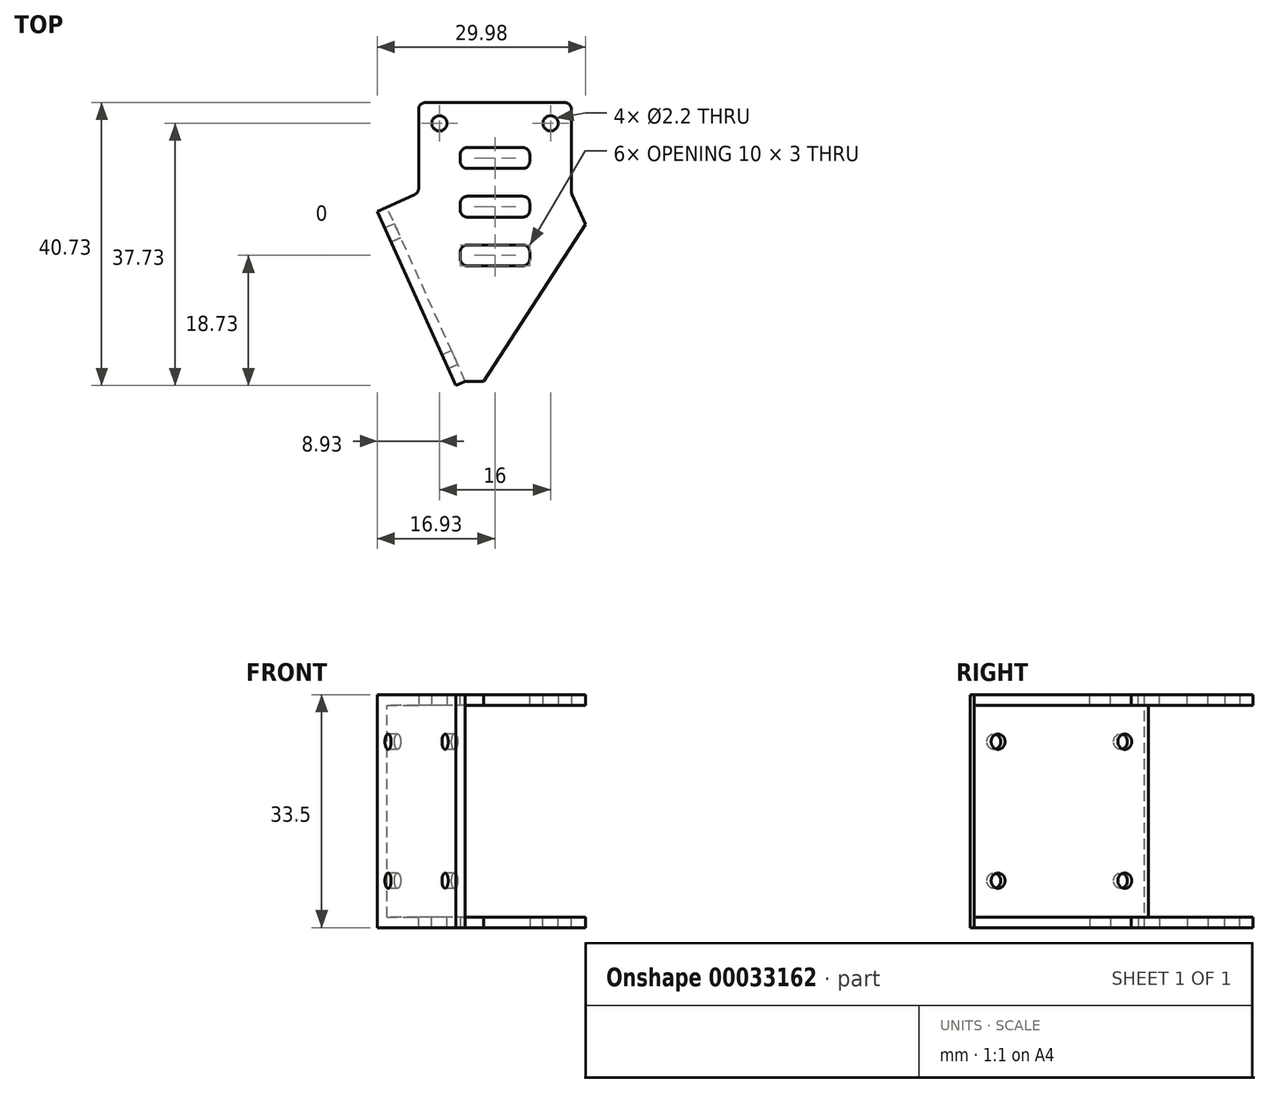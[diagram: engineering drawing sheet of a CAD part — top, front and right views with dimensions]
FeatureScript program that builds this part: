
annotation { "Feature Type Name" : "Feature", "Feature Type Description" : "" }
export const myFeature = defineFeature(function(context is Context, id is Id, definition is map)
    precondition{}
    {
        {
            var Q0;
            Q0=qCreatedBy(makeId("Top.planeOp"),FACE);
            var sketch = newSketch(context, id + "F0", { "sketchPlane" : qUnion([Q0])});
            skLineSegment(sketch, "E0.bottom", {"start": v(11, 16.5) * mm, "end": v(-11, 16.5) * mm});
            skLineSegment(sketch, "E0.top", {"start": v(11, -16.5) * mm, "end": v(-11, -16.5) * mm});
            skLineSegment(sketch, "E0.left", {"start": v(11, 16.5) * mm, "end": v(11, -16.5) * mm});
            skLineSegment(sketch, "E0.right", {"start": v(-11, 16.5) * mm, "end": v(-11, -16.5) * mm});
            skPoint(sketch, "E0.middle", {"position": v(0, 0) * mm});
            skCircle(sketch, "E1", {"center": v(8, 13.5) * mm, "radius": 1.1 * mm});
            skCircle(sketch, "E2.MirrorC", {"center": v(-8, 13.5) * mm, "radius": 1.1 * mm});
            skLineSegment(sketch, "E3", {"start": v(-11, 3.5) * mm, "end": v(-2, -16.5) * mm});
            skLineSegment(sketch, "E4.1.0.0", {"start": v(11, 3.5) * mm, "end": v(20, -16.5) * mm});
            skLineSegment(sketch, "E4.direction1", {"start": v(-2, -16.5) * mm, "end": v(20, -16.5) * mm, "construction": true});
            skLineSegment(sketch, "E5", {"start": v(11, -16.5) * mm, "end": v(20, -16.5) * mm});
            skSolve(sketch);
        }
        {
            var Q0;
            {var subQ4=sQuery(id+"F0.wireOp",EDGE,"E0.bottom");Q0=makeQuery(id+"F0.imprint","IMPRINT",FACE,{"disambiguationData":[TD([[makeQuery(id+"F0.imprint","IMPRINT",EDGE,{"derivedFrom":subQ4}),1.0]])]});}
            var Q1;
            {var subQ2=sQuery(id+"F0.wireOp",EDGE,"E4.1.0.0");Q1=makeQuery(id+"F0.imprint","IMPRINT",FACE,{"disambiguationData":[TD([[makeQuery(id+"F0.imprint","IMPRINT",EDGE,{"derivedFrom":subQ2}),-1.0]])]});}
            extrude(context, id + "F1", {"entities" : qUnion([Q0, Q1]), "depth" : 1.5 * mm});
        }
        {
            var Q0;
            Q0=makeQuery(id+"F1.opExtrude","CAP_FACE",FACE,{"disambiguationData":[OSD([sQuery(id+"F0.wireOp",EDGE,"E0.bottom"),sQuery(id+"F0.wireOp",EDGE,"E0.top"),sQuery(id+"F0.wireOp",EDGE,"E0.left"),sQuery(id+"F0.wireOp",EDGE,"E0.right"),sQuery(id+"F0.wireOp",EDGE,"E1"),sQuery(id+"F0.wireOp",EDGE,"E2.MirrorC"),sQuery(id+"F0.wireOp",EDGE,"E3"),sQuery(id+"F0.wireOp",EDGE,"E4.1.0.0"),sQuery(id+"F0.wireOp",EDGE,"E5")])],"isStart":false});
            var sketch = newSketch(context, id + "F2", { "sketchPlane" : qUnion([Q0])});
            skLineSegment(sketch, "E6", {"start": v(3, -16.5) * mm, "end": v(13.05, -1.06) * mm});
            skLineSegment(sketch, "E7", {"start": v(0, 16.5) * mm, "end": v(0, -16.5) * mm, "construction": true});
            skLineSegment(sketch, "E8.bottom", {"start": v(-4, 10) * mm, "end": v(4, 10) * mm});
            skLineSegment(sketch, "E8.top", {"start": v(-4, 7) * mm, "end": v(4, 7) * mm});
            skLineSegment(sketch, "E8.left", {"start": v(-5, 9) * mm, "end": v(-5, 8) * mm});
            skLineSegment(sketch, "E8.right", {"start": v(5, 9) * mm, "end": v(5, 8) * mm});
            skPoint(sketch, "E8.middle", {"position": v(0, 8.5) * mm});
            skPoint(sketch, "E9", {"position": v(-8, 13.5) * mm});
            skPoint(sketch, "E10.visualSharp", {"position": v(-5, 10) * mm});
            skArc(sketch, "E10.filletArc", {"start": v(-4, 10) * mm, "mid": v(-4.7, 9.7) * mm, "end": v(-5, 9) * mm});
            skPoint(sketch, "E11.visualSharp", {"position": v(-5, 7) * mm});
            skArc(sketch, "E11.filletArc", {"start": v(-5, 8) * mm, "mid": v(-4.7, 7.3) * mm, "end": v(-4, 7) * mm});
            skPoint(sketch, "E12.visualSharp", {"position": v(5, 10) * mm});
            skArc(sketch, "E12.filletArc", {"start": v(5, 9) * mm, "mid": v(4.7, 9.7) * mm, "end": v(4, 10) * mm});
            skPoint(sketch, "E13.visualSharp", {"position": v(5, 7) * mm});
            skArc(sketch, "E13.filletArc", {"start": v(4, 7) * mm, "mid": v(4.7, 7.3) * mm, "end": v(5, 8) * mm});
            skPoint(sketch, "E14.1.0.0", {"position": v(5, 3) * mm});
            skPoint(sketch, "E14.1.0.1", {"position": v(0, 1.5) * mm});
            skPoint(sketch, "E14.1.0.2", {"position": v(-5, 3) * mm});
            skPoint(sketch, "E14.1.0.3", {"position": v(-5, 0) * mm});
            skPoint(sketch, "E14.1.0.4", {"position": v(5, 0) * mm});
            skLineSegment(sketch, "E14.1.0.5", {"start": v(-4, 3) * mm, "end": v(4, 3) * mm});
            skLineSegment(sketch, "E14.1.0.6", {"start": v(-4, 0) * mm, "end": v(4, 0) * mm});
            skArc(sketch, "E14.1.0.7", {"start": v(4, 0) * mm, "mid": v(4.7, 0.3) * mm, "end": v(5, 1) * mm});
            skArc(sketch, "E14.1.0.8", {"start": v(5, 2) * mm, "mid": v(4.7, 2.7) * mm, "end": v(4, 3) * mm});
            skArc(sketch, "E14.1.0.9", {"start": v(-5, 1) * mm, "mid": v(-4.7, 0.3) * mm, "end": v(-4, 0) * mm});
            skLineSegment(sketch, "E14.1.0.10", {"start": v(-5, 2) * mm, "end": v(-5, 1) * mm});
            skLineSegment(sketch, "E14.1.0.11", {"start": v(5, 2) * mm, "end": v(5, 1) * mm});
            skArc(sketch, "E14.1.0.12", {"start": v(-4, 3) * mm, "mid": v(-4.7, 2.7) * mm, "end": v(-5, 2) * mm});
            skLineSegment(sketch, "E14.direction1", {"start": v(-5, 7) * mm, "end": v(-5, 0) * mm, "construction": true});
            skPoint(sketch, "E15.0.2.0", {"position": v(5, -4) * mm});
            skPoint(sketch, "E15.1.2.0", {"position": v(0, -5.5) * mm});
            skPoint(sketch, "E15.2.2.0", {"position": v(-5, -4) * mm});
            skPoint(sketch, "E15.3.2.0", {"position": v(-5, -7) * mm});
            skPoint(sketch, "E15.4.2.0", {"position": v(5, -7) * mm});
            skLineSegment(sketch, "E15.5.2.0", {"start": v(-4, -4) * mm, "end": v(4, -4) * mm});
            skLineSegment(sketch, "E15.8.2.0", {"start": v(-4, -7) * mm, "end": v(4, -7) * mm});
            skArc(sketch, "E15.11.2.0", {"start": v(4, -7) * mm, "mid": v(4.7, -6.7) * mm, "end": v(5, -6) * mm});
            skArc(sketch, "E15.15.2.0", {"start": v(5, -5) * mm, "mid": v(4.7, -4.3) * mm, "end": v(4, -4) * mm});
            skArc(sketch, "E15.19.2.0", {"start": v(-5, -6) * mm, "mid": v(-4.7, -6.7) * mm, "end": v(-4, -7) * mm});
            skLineSegment(sketch, "E15.23.2.0", {"start": v(-5, -5) * mm, "end": v(-5, -6) * mm});
            skLineSegment(sketch, "E15.26.2.0", {"start": v(5, -5) * mm, "end": v(5, -6) * mm});
            skArc(sketch, "E15.29.2.0", {"start": v(-4, -4) * mm, "mid": v(-4.7, -4.3) * mm, "end": v(-5, -5) * mm});
            skSolve(sketch);
        }
        {
            var Q0;
            {var subQ0=sQuery(id+"F2.wireOp",EDGE,"E6");Q0=makeQuery(id+"F2.imprint","IMPRINT",FACE,{"disambiguationData":[TD([[makeQuery(id+"F2.imprint","IMPRINT",EDGE,{"derivedFrom":subQ0}),-1.0]])]});}
            var Q1;
            Q1=makeQuery(id+"F2.imprint","IMPRINT",FACE,{"disambiguationData":[TD([[makeQuery(id+"F2.imprint","IMPRINT",EDGE,{"derivedFrom":sQuery(id+"F2.wireOp",EDGE,"E8.bottom")}),-1.0]])]});
            var Q2;
            Q2=makeQuery(id+"F2.imprint","IMPRINT",FACE,{"disambiguationData":[TD([[makeQuery(id+"F2.imprint","IMPRINT",EDGE,{"derivedFrom":sQuery(id+"F2.wireOp",EDGE,"E14.1.0.5")}),-1.0]])]});
            var Q3;
            Q3=makeQuery(id+"F2.imprint","IMPRINT",FACE,{"disambiguationData":[TD([[makeQuery(id+"F2.imprint","IMPRINT",EDGE,{"derivedFrom":sQuery(id+"F2.wireOp",EDGE,"E15.5.2.0")}),-1.0]])]});
            extrude(context, id + "F3", {"entities" : qUnion([Q0, Q1, Q2, Q3]), "operationType" : NewBodyOperationType.REMOVE, "endBound" : BoundingType.UP_TO_NEXT, "oppositeDirection" : true, "depth" : 25 * mm});
        }
        {
            var Q0;
            Q0=makeQuery(id+"F1.opExtrude","SWEPT_FACE",FACE,{"disambiguationData":[OSD([sQuery(id+"F0.wireOp",EDGE,"E3")])]});
            var sketch = newSketch(context, id + "F4", { "sketchPlane" : qUnion([Q0])});
            skLineSegment(sketch, "E16.bottom", {"start": v(-7.7, 0) * mm, "end": v(14.23, 0) * mm});
            skLineSegment(sketch, "E16.top", {"start": v(-7.7, 1.5) * mm, "end": v(14.23, 1.5) * mm});
            skLineSegment(sketch, "E16.left", {"start": v(-7.7, 0) * mm, "end": v(-7.7, 1.5) * mm});
            skLineSegment(sketch, "E16.right", {"start": v(14.23, 0) * mm, "end": v(14.23, 1.5) * mm});
            skSolve(sketch);
        }
        {
            var Q0;
            Q0 = qSketchRegion(id + "F4", true);
            extrude(context, id + "F5", {"entities" : qUnion([Q0]), "operationType" : NewBodyOperationType.ADD, "depth" : 5 * mm});
        }
        {
            var Q0;
            Q0=makeQuery(id+"F5.boolean.opBoolean","MERGE",FACE,{"derivedFrom":[makeQuery(id+"F1.opExtrude","CAP_FACE",FACE,{"disambiguationData":[OSD([sQuery(id+"F0.wireOp",EDGE,"E0.bottom"),sQuery(id+"F0.wireOp",EDGE,"E0.top"),sQuery(id+"F0.wireOp",EDGE,"E0.left"),sQuery(id+"F0.wireOp",EDGE,"E0.right"),sQuery(id+"F0.wireOp",EDGE,"E1"),sQuery(id+"F0.wireOp",EDGE,"E2.MirrorC"),sQuery(id+"F0.wireOp",EDGE,"E3"),sQuery(id+"F0.wireOp",EDGE,"E4.1.0.0"),sQuery(id+"F0.wireOp",EDGE,"E5")])],"isStart":false}),makeQuery(id+"F5.opExtrude","SWEPT_FACE",FACE,{"disambiguationData":[OSD([sQuery(id+"F4.wireOp",EDGE,"E16.top")])]})]});
            var sketch = newSketch(context, id + "F6", { "sketchPlane" : qUnion([Q0])});
            skLineSegment(sketch, "E17", {"start": v(-6.56, -18.55) * mm, "end": v(-4.28, -23.62) * mm});
            skPoint(sketch, "E17.endSnap0", {"position": v(-4.28, -17.53) * mm});
            skLineSegment(sketch, "E18", {"start": v(3, -16.5) * mm, "end": v(3, -23.62) * mm});
            skLineSegment(sketch, "E19", {"start": v(-4.28, -23.62) * mm, "end": v(3, -23.62) * mm});
            skLineSegment(sketch, "E20", {"start": v(-6.56, -18.55) * mm, "end": v(-2, -16.5) * mm});
            skLineSegment(sketch, "E21", {"start": v(-2, -16.5) * mm, "end": v(3, -16.5) * mm});
            skSolve(sketch);
        }
        {
            var Q0;
            Q0 = qSketchRegion(id + "F6", true);
            extrude(context, id + "F7", {"entities" : qUnion([Q0]), "operationType" : NewBodyOperationType.ADD, "oppositeDirection" : true, "depth" : 1.5 * mm});
        }
        {
            var Q0;
            Q0=makeQuery(id+"F7.boolean.opBoolean","MERGE",FACE,{"derivedFrom":[makeQuery(id+"F5.boolean.opBoolean","MERGE",FACE,{"derivedFrom":[makeQuery(id+"F1.opExtrude","CAP_FACE",FACE,{"disambiguationData":[OSD([sQuery(id+"F0.wireOp",EDGE,"E0.bottom"),sQuery(id+"F0.wireOp",EDGE,"E0.top"),sQuery(id+"F0.wireOp",EDGE,"E0.left"),sQuery(id+"F0.wireOp",EDGE,"E0.right"),sQuery(id+"F0.wireOp",EDGE,"E1"),sQuery(id+"F0.wireOp",EDGE,"E2.MirrorC"),sQuery(id+"F0.wireOp",EDGE,"E3"),sQuery(id+"F0.wireOp",EDGE,"E4.1.0.0"),sQuery(id+"F0.wireOp",EDGE,"E5")])],"isStart":false}),makeQuery(id+"F5.opExtrude","SWEPT_FACE",FACE,{"disambiguationData":[OSD([sQuery(id+"F4.wireOp",EDGE,"E16.top")])]})]}),makeQuery(id+"F7.opExtrude","CAP_FACE",FACE,{"disambiguationData":[OSD([sQuery(id+"F6.wireOp",EDGE,"E17"),sQuery(id+"F6.wireOp",EDGE,"E18"),sQuery(id+"F6.wireOp",EDGE,"E19"),sQuery(id+"F6.wireOp",EDGE,"E20"),sQuery(id+"F6.wireOp",EDGE,"E21")])],"isStart":true})]});
            var sketch = newSketch(context, id + "F8", { "sketchPlane" : qUnion([Q0])});
            skLineSegment(sketch, "E22", {"start": v(13.05, -1.06) * mm, "end": v(-1.63, -23.62) * mm});
            skLineSegment(sketch, "E23", {"start": v(-1.63, -23.62) * mm, "end": v(3, -23.62) * mm});
            skLineSegment(sketch, "E24", {"start": v(3, -23.62) * mm, "end": v(3, -16.5) * mm});
            skSolve(sketch);
        }
        {
            var Q0;
            Q0 = qSketchRegion(id + "F8", true);
            extrude(context, id + "F9", {"entities" : qUnion([Q0]), "operationType" : NewBodyOperationType.REMOVE, "endBound" : BoundingType.UP_TO_NEXT, "oppositeDirection" : true, "depth" : 25 * mm});
        }
        {
            var Q0;
            Q0=makeQuery(id+"F1.opExtrude","SWEPT_EDGE",EDGE,{"disambiguationData":[OSD([sQuery(id+"F0.wireOp",EDGE,"E0.bottom"),sQuery(id+"F0.wireOp",EDGE,"E0.right")])]});
            var Q1;
            Q1=makeQuery(id+"F1.opExtrude","SWEPT_EDGE",EDGE,{"disambiguationData":[OSD([sQuery(id+"F0.wireOp",EDGE,"E0.bottom"),sQuery(id+"F0.wireOp",EDGE,"E0.left")])]});
            var Q2;
            Q2=makeQuery(id+"F5.boolean.opBoolean","MERGE",EDGE,{"derivedFrom":[makeQuery(id+"F1.opExtrude","SWEPT_EDGE",EDGE,{"disambiguationData":[OSD([sQuery(id+"F0.wireOp",EDGE,"E0.right"),sQuery(id+"F0.wireOp",EDGE,"E3")])]}),makeQuery(id+"F5.opExtrude","CAP_EDGE",EDGE,{"disambiguationData":[OSD([sQuery(id+"F4.wireOp",EDGE,"E16.left")])],"isStart":true})]});
            var Q3;
            Q3=makeQuery(id+"F9.boolean.opBoolean","COPY",EDGE,{"derivedFrom":makeQuery(id+"F9.opExtrude","SWEPT_EDGE",EDGE,{"disambiguationData":[OSD([sQuery(id+"F6.wireOp",EDGE,"E19"),sQuery(id+"F8.wireOp",EDGE,"E22"),sQuery(id+"F8.wireOp",EDGE,"E23")])]})});
            var Q4;
            Q4=makeQuery(id+"F3.boolean.opBoolean","COPY",EDGE,{"derivedFrom":makeQuery(id+"F3.opExtrude","SWEPT_EDGE",EDGE,{"disambiguationData":[OSD([sQuery(id+"F0.wireOp",EDGE,"E4.1.0.0"),sQuery(id+"F2.wireOp",EDGE,"E6")])]})});
            var Q5;
            Q5=makeQuery(id+"F1.opExtrude","SWEPT_EDGE",EDGE,{"disambiguationData":[OSD([sQuery(id+"F0.wireOp",EDGE,"E0.left"),sQuery(id+"F0.wireOp",EDGE,"E4.1.0.0")])]});
            fillet(context, id + "F10", {"entities" : qUnion([Q0, Q1, Q2, Q3, Q4, Q5]), "radius" : 1 * mm, "tangentPropagation" : true, "allowEdgeOverflow" : false});
        }
        {
            var Q0;
            Q0=makeQuery(id+"F7.boolean.opBoolean","MERGE",FACE,{"derivedFrom":[makeQuery(id+"F5.opExtrude","CAP_FACE",FACE,{"disambiguationData":[OSD([sQuery(id+"F4.wireOp",EDGE,"E16.bottom"),sQuery(id+"F4.wireOp",EDGE,"E16.top"),sQuery(id+"F4.wireOp",EDGE,"E16.left"),sQuery(id+"F4.wireOp",EDGE,"E16.right")])],"isStart":false}),makeQuery(id+"F7.opExtrude","SWEPT_FACE",FACE,{"disambiguationData":[OSD([sQuery(id+"F6.wireOp",EDGE,"E17")])]})]});
            var sketch = newSketch(context, id + "F11", { "sketchPlane" : qUnion([Q0])});
            skLineSegment(sketch, "E25.bottom", {"start": v(-7.7, 1.5) * mm, "end": v(19.78, 1.5) * mm});
            skLineSegment(sketch, "E25.top", {"start": v(-7.7, 0) * mm, "end": v(19.78, 0) * mm});
            skLineSegment(sketch, "E25.left", {"start": v(-7.7, 1.5) * mm, "end": v(-7.7, 0) * mm});
            skLineSegment(sketch, "E25.right", {"start": v(19.78, 1.5) * mm, "end": v(19.78, 0) * mm});
            skSolve(sketch);
        }
        {
            var Q0;
            Q0 = qSketchRegion(id + "F11", true);
            extrude(context, id + "F12", {"entities" : qUnion([Q0]), "operationType" : NewBodyOperationType.ADD, "depth" : 1.5 * mm});
        }
        {
            var Q0;
            Q0=makeQuery(id+"F12.boolean.opBoolean","MERGE",FACE,{"derivedFrom":[makeQuery(id+"F7.boolean.opBoolean","MERGE",FACE,{"derivedFrom":[makeQuery(id+"F5.boolean.opBoolean","MERGE",FACE,{"derivedFrom":[makeQuery(id+"F1.opExtrude","CAP_FACE",FACE,{"disambiguationData":[OSD([sQuery(id+"F0.wireOp",EDGE,"E0.bottom"),sQuery(id+"F0.wireOp",EDGE,"E0.top"),sQuery(id+"F0.wireOp",EDGE,"E0.left"),sQuery(id+"F0.wireOp",EDGE,"E0.right"),sQuery(id+"F0.wireOp",EDGE,"E1"),sQuery(id+"F0.wireOp",EDGE,"E2.MirrorC"),sQuery(id+"F0.wireOp",EDGE,"E3"),sQuery(id+"F0.wireOp",EDGE,"E4.1.0.0"),sQuery(id+"F0.wireOp",EDGE,"E5")])],"isStart":true}),makeQuery(id+"F5.opExtrude","SWEPT_FACE",FACE,{"disambiguationData":[OSD([sQuery(id+"F4.wireOp",EDGE,"E16.bottom")])]})]}),makeQuery(id+"F7.opExtrude","CAP_FACE",FACE,{"disambiguationData":[OSD([sQuery(id+"F6.wireOp",EDGE,"E17"),sQuery(id+"F6.wireOp",EDGE,"E18"),sQuery(id+"F6.wireOp",EDGE,"E19"),sQuery(id+"F6.wireOp",EDGE,"E20"),sQuery(id+"F6.wireOp",EDGE,"E21")])],"isStart":false})]}),makeQuery(id+"F12.opExtrude","SWEPT_FACE",FACE,{"disambiguationData":[OSD([sQuery(id+"F11.wireOp",EDGE,"E25.top")])]})]});
            var sketch = newSketch(context, id + "F13", { "sketchPlane" : qUnion([Q0])});
            skLineSegment(sketch, "E26", {"start": v(-4.28, 23.62) * mm, "end": v(-15.56, -1.45) * mm});
            skLineSegment(sketch, "E27", {"start": v(-15.56, -1.45) * mm, "end": v(-16.93, -0.83) * mm});
            skLineSegment(sketch, "E28", {"start": v(-16.93, -0.83) * mm, "end": v(-5.65, 24.23) * mm});
            skLineSegment(sketch, "E29", {"start": v(-5.65, 24.23) * mm, "end": v(-4.28, 23.62) * mm});
            skSolve(sketch);
        }
        {
            var Q0;
            Q0 = qSketchRegion(id + "F13", true);
            extrude(context, id + "F14", {"entities" : qUnion([Q0]), "operationType" : NewBodyOperationType.ADD, "depth" : (30.5 + 1.5) * mm});
        }
        {
            var Q0;
            Q0=qCreatedBy(makeId("Top.planeOp"),FACE);
            cPlane(context, id + "F15", {"entities" : qUnion([Q0]), "cplaneType" : CPlaneType.OFFSET, "offset" : (30.5 / 2) * mm, "oppositeDirection" : true, "width" : 150 * mm, "height" : 150 * mm});
        }
        {
            var Q0;
            Q0=makeQuery(id+"F1.opExtrude","SWEPT_BODY",BODY,{"disambiguationData":[OSD([sQuery(id+"F0.wireOp",EDGE,"E0.bottom"),sQuery(id+"F0.wireOp",EDGE,"E0.top"),sQuery(id+"F0.wireOp",EDGE,"E0.left"),sQuery(id+"F0.wireOp",EDGE,"E0.right"),sQuery(id+"F0.wireOp",EDGE,"E1"),sQuery(id+"F0.wireOp",EDGE,"E2.MirrorC"),sQuery(id+"F0.wireOp",EDGE,"E3"),sQuery(id+"F0.wireOp",EDGE,"E4.1.0.0"),sQuery(id+"F0.wireOp",EDGE,"E5")])]});
            var Q1;
            Q1=qCreatedBy(id+"F15.planeOp",FACE);
            mirror(context, id + "F16", {"operationType" : NewBodyOperationType.ADD, "entities" : qUnion([Q0]), "mirrorPlane" : qUnion([Q1])});
        }
        {
            var Q0;
            Q0=makeQuery(id+"F14.boolean.opBoolean","MERGE",FACE,{"derivedFrom":[makeQuery(id+"F12.opExtrude","CAP_FACE",FACE,{"disambiguationData":[OSD([sQuery(id+"F11.wireOp",EDGE,"E25.bottom"),sQuery(id+"F11.wireOp",EDGE,"E25.top"),sQuery(id+"F11.wireOp",EDGE,"E25.left"),sQuery(id+"F11.wireOp",EDGE,"E25.right")])],"isStart":false}),makeQuery(id+"F14.opExtrude","SWEPT_FACE",FACE,{"disambiguationData":[OSD([sQuery(id+"F13.wireOp",EDGE,"E28")])]})]});
            var sketch = newSketch(context, id + "F17", { "sketchPlane" : qUnion([Q0])});
            skLineSegment(sketch, "E30", {"start": v(6.04, -32) * mm, "end": v(6.04, 1.5) * mm, "construction": true});
            skCircle(sketch, "E31", {"center": v(-3.96, -25.25) * mm, "radius": 1.1 * mm});
            skCircle(sketch, "E32.MirrorC", {"center": v(16.04, -25.25) * mm, "radius": 1.1 * mm});
            skCircle(sketch, "E33.MirrorC", {"center": v(-3.96, -5.25) * mm, "radius": 1.1 * mm});
            skCircle(sketch, "E34.MirrorC", {"center": v(16.04, -5.25) * mm, "radius": 1.1 * mm});
            skSolve(sketch);
        }
        {
            var Q0;
            Q0 = qSketchRegion(id + "F17", true);
            extrude(context, id + "F18", {"entities" : qUnion([Q0]), "operationType" : NewBodyOperationType.REMOVE, "endBound" : BoundingType.UP_TO_NEXT, "oppositeDirection" : true, "depth" : 25 * mm});
        }
    });
